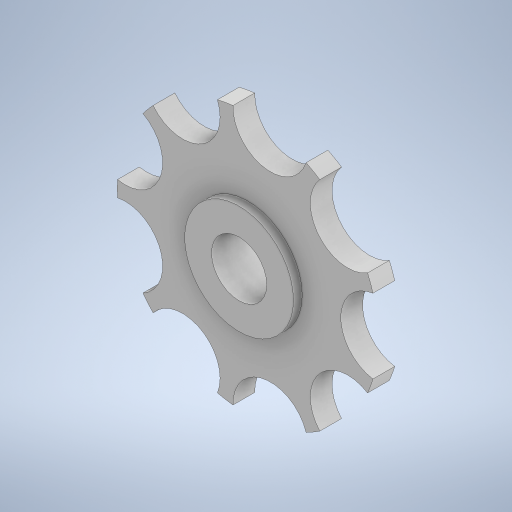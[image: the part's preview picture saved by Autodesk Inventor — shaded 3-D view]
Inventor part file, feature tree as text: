
AUTODESK INVENTOR PART (.ipt)
format: ipt  version: 2024 (Build 280153000, 153)  size: 306,176 bytes
history: native  units: mm
features: extrude x4, sketch x4
ambient origin geometry x8: Origin, YZ Plane, XZ Plane, XY Plane, X Axis, Y Axis, Z Axis, Center Point
bodies: Solid1 (feature_tree)
feature tree (8):
  extrude  "Extrusion1"  Depth=12.7mm
  extrude  "Extrusion2"  Depth=90.0mm TaperAngle=360.0deg
  extrude  "Extrusion3"  Depth=5.0mm
  extrude  "Extrusion4"  Depth=2.0mm
  sketch  "Sketch1"  dims[d0=60.0mm d1=12.7mm]
  sketch  "Sketch2"  dims[d2=52.4mm d3=90.0mm d5=360.0deg]
  sketch  "Sketch3"  dims[d7=5.0mm d8=0.0mm d9=12.7mm]
  sketch  "Sketch4"  dims[d10=0.0mm d11=0.0mm d12=25.0mm d13=12.7mm d14=2.0mm d15=0.0mm d16=12.7mm d17=25.0mm d18=2.0mm d19=0.0mm]
